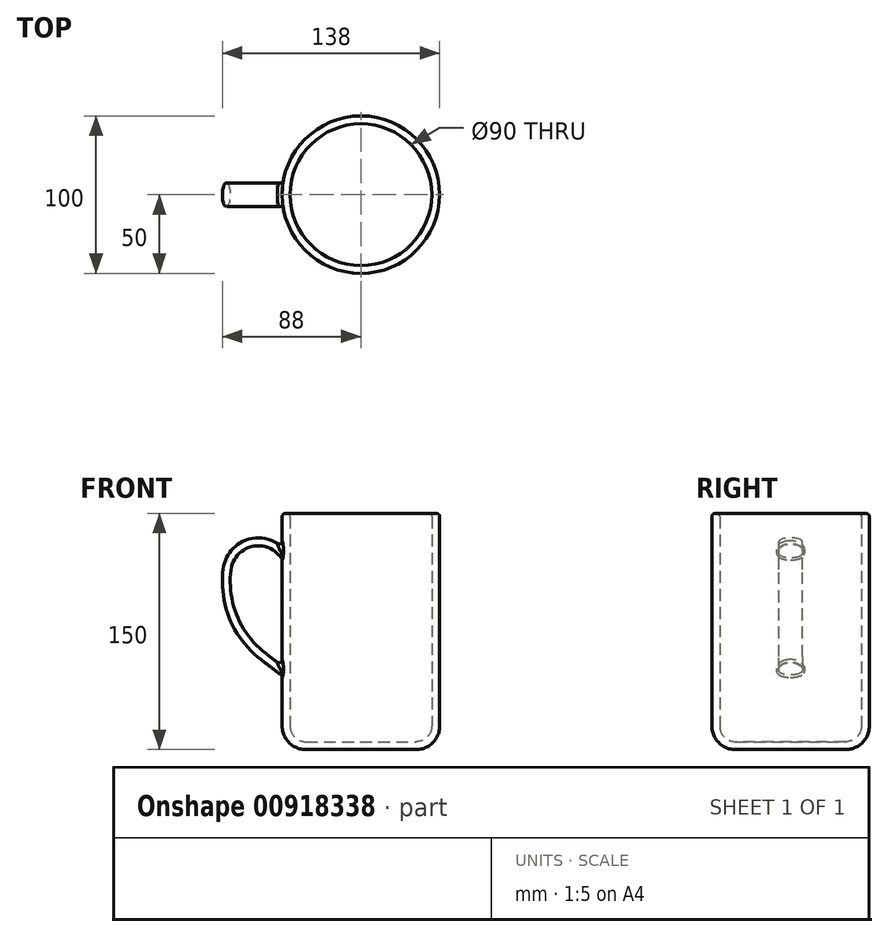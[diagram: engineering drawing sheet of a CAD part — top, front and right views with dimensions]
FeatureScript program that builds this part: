
annotation { "Feature Type Name" : "Feature", "Feature Type Description" : "" }
export const myFeature = defineFeature(function(context is Context, id is Id, definition is map)
    precondition{}
    {
        {
            var Q0;
            Q0=qCreatedBy(makeId("Front.planeOp"),FACE);
            var sketch = newSketch(context, id + "F0", { "sketchPlane" : qUnion([Q0])});
            skLineSegment(sketch, "E0", {"start": v(-45, 15) * mm, "end": v(-45, 150) * mm});
            skLineSegment(sketch, "E1", {"start": v(-45, 150) * mm, "end": v(-50, 150) * mm});
            skLineSegment(sketch, "E2", {"start": v(-50, 150) * mm, "end": v(-50, 15) * mm});
            skArc(sketch, "E3", {"start": v(-50, 15) * mm, "mid": v(-45.6, 4.4) * mm, "end": v(-35, 0) * mm});
            skArc(sketch, "E4", {"start": v(-45, 15) * mm, "mid": v(-42.07, 7.93) * mm, "end": v(-35, 5) * mm});
            skLineSegment(sketch, "E5", {"start": v(-35, 5) * mm, "end": v(0, 5) * mm});
            skLineSegment(sketch, "E6", {"start": v(-35, 0) * mm, "end": v(0, 0) * mm});
            skLineSegment(sketch, "E7", {"start": v(0, 0) * mm, "end": v(0, 5) * mm});
            skSolve(sketch);
        }
        {
            var Q0;
            Q0 = qSketchRegion(id + "F0", true);
            var Q1;
            Q1=sQuery(id+"F0.wireOp",EDGE,"E7");
            revolve(context, id + "F1", {"surfaceOperationType" : NewSurfaceOperationType.NEW, "entities" : qUnion([Q0]), "axis" : qUnion([Q1]), "revolveType" : RevolveType.FULL});
        }
        {
            var Q0;
            Q0=qCreatedBy(makeId("Front.planeOp"),FACE);
            var sketch = newSketch(context, id + "F2", { "sketchPlane" : qUnion([Q0])});
            skLineSegment(sketch, "E8", {"start": v(-61.92, 59.1) * mm, "end": v(-50, 50) * mm});
            skArc(sketch, "E9", {"start": v(-61.92, 59.1) * mm, "mid": v(-80.9, 83.73) * mm, "end": v(-85, 114.55) * mm});
            skArc(sketch, "E10", {"start": v(-85, 114.55) * mm, "mid": v(-70.89, 131.13) * mm, "end": v(-50, 125) * mm});
            skLineSegment(sketch, "E11", {"start": v(-50, 125) * mm, "end": v(-39.63, 112.93) * mm});
            skLineSegment(sketch, "E12", {"start": v(-50, 50) * mm, "end": v(-30.12, 34.82) * mm});
            skSolve(sketch);
        }
        {
            var Q0;
            Q0=sQuery(id+"F2.wireOp",EDGE,"E8");
            var Q1;
            Q1=sQuery(id+"F2.wireOp",VERTEX,"E8.end");
            cPlane(context, id + "F3", {"entities" : qUnion([Q0, Q1]), "cplaneType" : CPlaneType.LINE_POINT, "offset" : 25 * mm, "width" : 150 * mm, "height" : 150 * mm});
        }
        {
            var Q0;
            Q0=qCreatedBy(id+"F3.planeOp",FACE);
            var sketch = newSketch(context, id + "F4", { "sketchPlane" : qUnion([Q0])});
            skEllipse(sketch, "E13", {"center": v(0, 9.39) * mm, "majorRadius": 7.5 * mm, "minorRadius": 2.5 * mm, "majorAxis": v(-1, 0)});
            skSolve(sketch);
        }
        {
            var Q0;
            Q0 = qSketchRegion(id + "F4", true);
            var Q1;
            Q1=sQuery(id+"F2.wireOp",EDGE,"E8");
            var Q2;
            Q2=sQuery(id+"F2.wireOp",EDGE,"E9");
            var Q3;
            Q3=sQuery(id+"F2.wireOp",EDGE,"E10");
            var Q4;
            Q4=sQuery(id+"F2.wireOp",EDGE,"E11");
            var Q5;
            Q5=sQuery(id+"F2.wireOp",EDGE,"E12");
            sweep(context, id + "F5", {"operationType" : NewBodyOperationType.ADD, "profiles" : qUnion([Q0]), "path" : qUnion([Q1, Q2, Q3, Q4, Q5])});
        }
        {
            var Q0;
            Q0=makeQuery(id+"F1.opRevolve","SWEPT_FACE",FACE,{"disambiguationData":[OSD([sQuery(id+"F0.wireOp",EDGE,"E1")])]});
            var sketch = newSketch(context, id + "F6", { "sketchPlane" : qUnion([Q0])});
            skCircle(sketch, "E14.0", {"center": v(0, 0) * mm, "radius": 45 * mm});
            skSolve(sketch);
        }
        {
            var Q0;
            Q0=makeQuery(id+"F6.imprint","IMPRINT",FACE,{"disambiguationData":[TD([[makeQuery(id+"F6.imprint","IMPRINT",EDGE,{"derivedFrom":sQuery(id+"F6.wireOp",EDGE,"E14.0")}),-1.0]])]});
            extrude(context, id + "F7", {"entities" : qUnion([Q0]), "operationType" : NewBodyOperationType.REMOVE, "endBound" : BoundingType.UP_TO_NEXT, "oppositeDirection" : true, "depth" : 25 * mm, "offsetDistance" : 25 * mm});
        }
        {
            var Q0;
            Q0=makeQuery(id+"F1.opRevolve","SWEPT_EDGE",EDGE,{"disambiguationData":[OSD([sQuery(id+"F0.wireOp",EDGE,"E1"),sQuery(id+"F0.wireOp",EDGE,"E2")])]});
            var Q1;
            Q1=makeQuery(id+"F1.opRevolve","SWEPT_EDGE",EDGE,{"disambiguationData":[OSD([sQuery(id+"F0.wireOp",EDGE,"E0"),sQuery(id+"F0.wireOp",EDGE,"E1")])]});
            var Q2;
            Q2=makeQuery(id+"F5.boolean.opBoolean","INTERSECT",EDGE,{"derivedFrom":[makeQuery(id+"F1.opRevolve","SWEPT_FACE",FACE,{"disambiguationData":[OSD([sQuery(id+"F0.wireOp",EDGE,"E2")])]}),makeQuery(id+"F5.opSweep","SWEPT_FACE",FACE,{"disambiguationData":[OSD([sQuery(id+"F2.wireOp",EDGE,"E10"),sQuery(id+"F4.wireOp",EDGE,"E13")])]})]});
            var Q3;
            Q3=makeQuery(id+"F5.boolean.opBoolean","INTERSECT",EDGE,{"derivedFrom":[makeQuery(id+"F1.opRevolve","SWEPT_FACE",FACE,{"disambiguationData":[OSD([sQuery(id+"F0.wireOp",EDGE,"E2")])]}),makeQuery(id+"F5.opSweep","SWEPT_FACE",FACE,{"disambiguationData":[OSD([sQuery(id+"F2.wireOp",EDGE,"E8"),sQuery(id+"F4.wireOp",EDGE,"E13")])]})]});
            fillet(context, id + "F8", {"entities" : qUnion([Q0, Q1, Q2, Q3]), "radius" : 2 * mm, "tangentPropagation" : true, "allowEdgeOverflow" : false});
        }
    });
